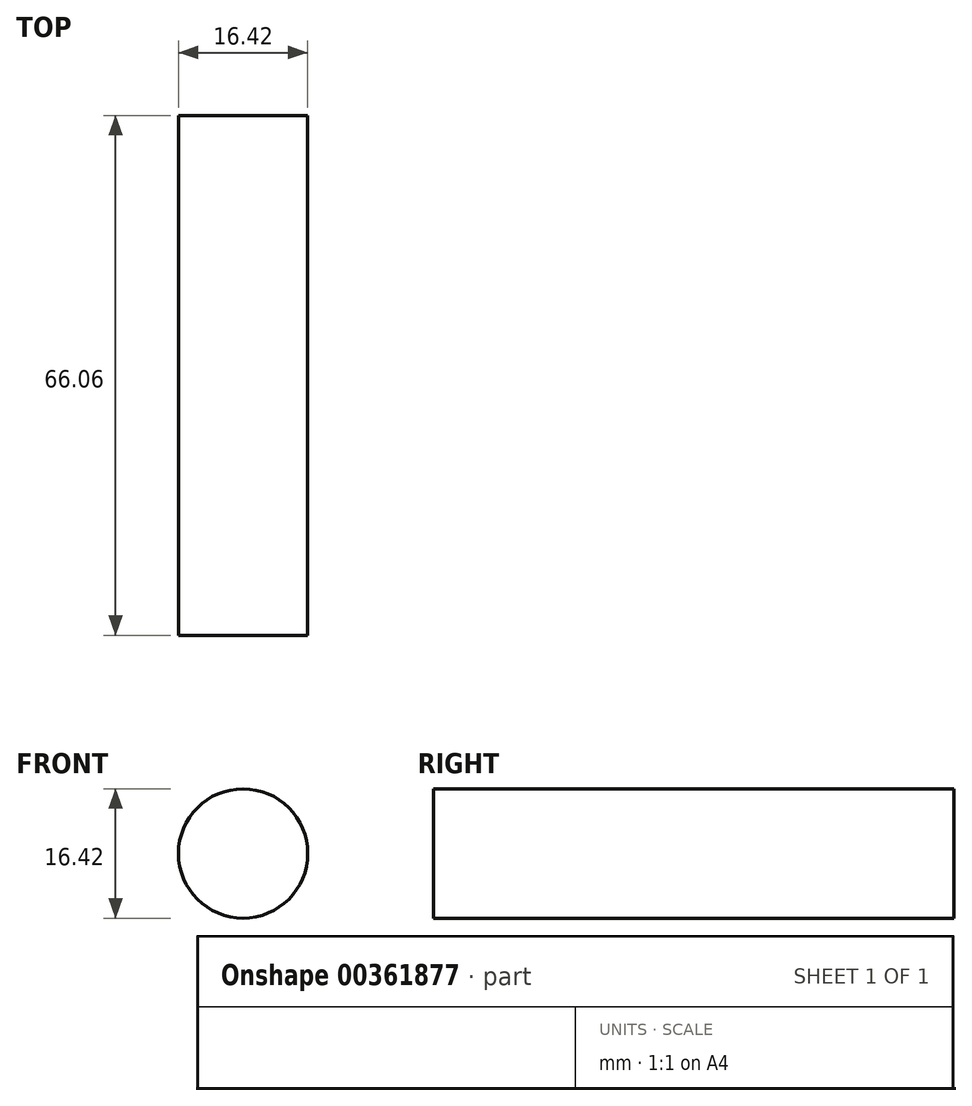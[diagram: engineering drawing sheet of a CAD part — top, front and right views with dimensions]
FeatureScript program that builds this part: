
annotation { "Feature Type Name" : "Feature", "Feature Type Description" : "" }
export const myFeature = defineFeature(function(context is Context, id is Id, definition is map)
    precondition{}
    {
        {
            var Q0;
            Q0=qCreatedBy(makeId("Right.planeOp"),FACE);
            var sketch = newSketch(context, id + "F0", { "sketchPlane" : qUnion([Q0])});
            skLineSegment(sketch, "E0.bottom", {"start": v(-33.03, 0) * mm, "end": v(33.03, 0) * mm});
            skLineSegment(sketch, "E0.top", {"start": v(-33.03, -8.21) * mm, "end": v(33.03, -8.21) * mm});
            skLineSegment(sketch, "E0.left", {"start": v(-33.03, 0) * mm, "end": v(-33.03, -8.21) * mm});
            skLineSegment(sketch, "E0.right", {"start": v(33.03, 0) * mm, "end": v(33.03, -8.21) * mm});
            skSolve(sketch);
        }
        {
            var Q0;
            Q0=makeQuery(id+"F0.imprint","IMPRINT",FACE,{"disambiguationData":[TD([[makeQuery(id+"F0.imprint","IMPRINT",EDGE,{"derivedFrom":sQuery(id+"F0.wireOp",EDGE,"E0.bottom")}),-1.0]])]});
            var Q1;
            Q1=sQuery(id+"F0.wireOp",EDGE,"E0.bottom");
            revolve(context, id + "F1", {"entities" : qUnion([Q0]), "axis" : qUnion([Q1]), "revolveType" : RevolveType.FULL});
        }
    });
